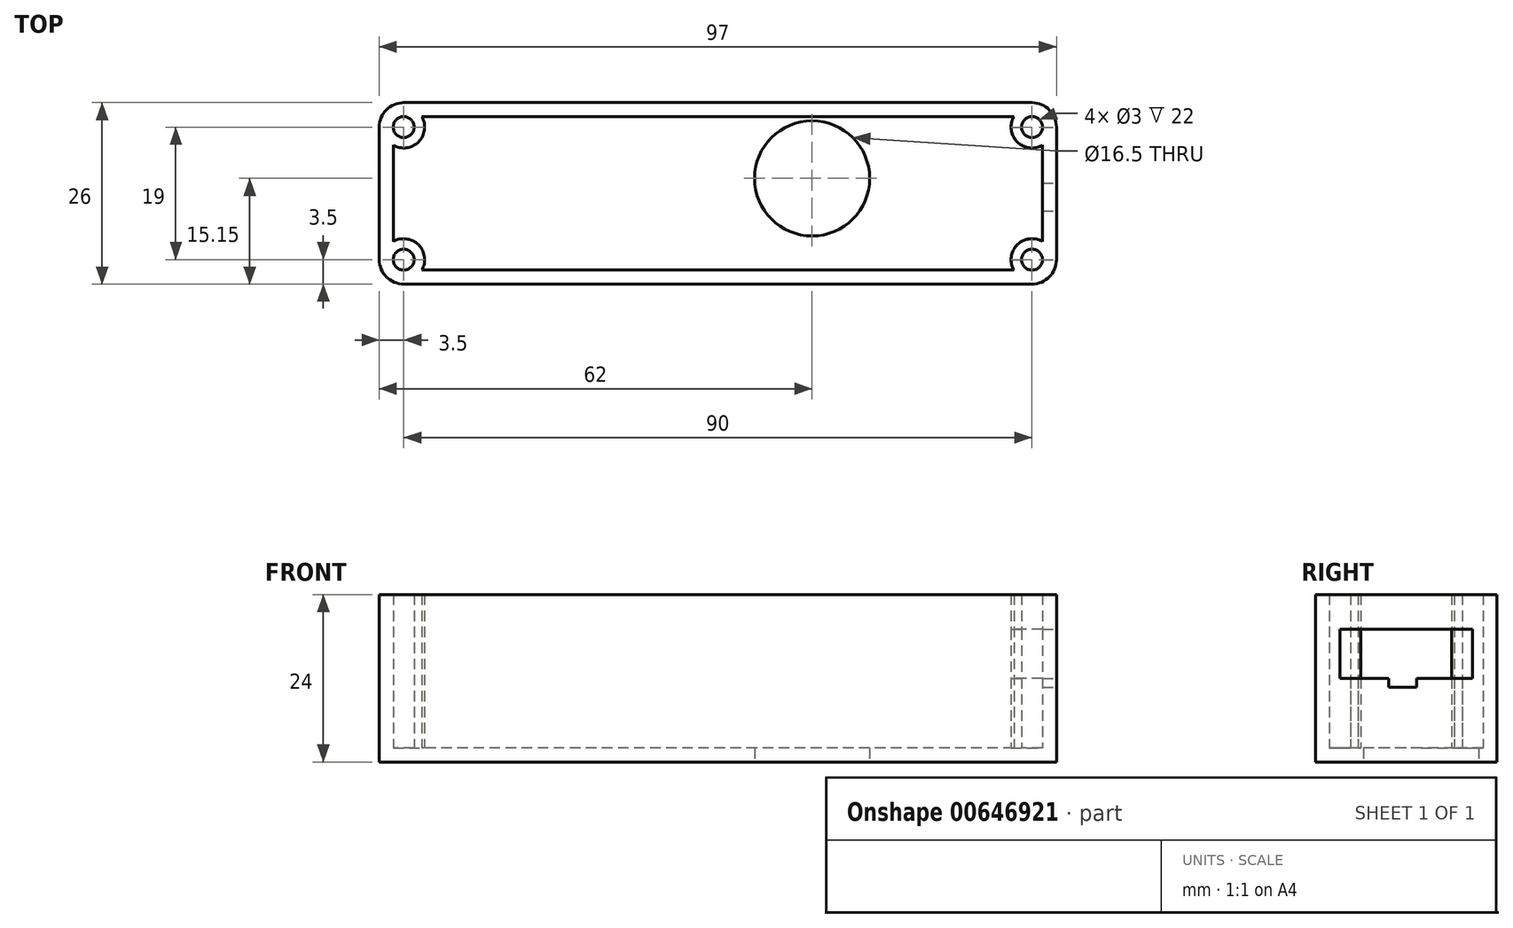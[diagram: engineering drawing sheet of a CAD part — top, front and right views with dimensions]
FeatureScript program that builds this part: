
annotation { "Feature Type Name" : "Feature", "Feature Type Description" : "" }
export const myFeature = defineFeature(function(context is Context, id is Id, definition is map)
    precondition{}
    {
        {
            var Q0;
            Q0=qCreatedBy(makeId("Top.planeOp"),FACE);
            var sketch = newSketch(context, id + "F0", { "sketchPlane" : qUnion([Q0])});
            skLineSegment(sketch, "E0.bottom", {"start": v(45, 13) * mm, "end": v(-45, 13) * mm});
            skLineSegment(sketch, "E0.top", {"start": v(45, -13) * mm, "end": v(-45, -13) * mm});
            skLineSegment(sketch, "E0.left", {"start": v(48.5, 9.5) * mm, "end": v(48.5, -9.5) * mm});
            skLineSegment(sketch, "E0.right", {"start": v(-48.5, 9.5) * mm, "end": v(-48.5, -9.5) * mm});
            skPoint(sketch, "E0.middle", {"position": v(0, 0) * mm});
            skPoint(sketch, "E1.visualSharp", {"position": v(48.5, 13) * mm});
            skArc(sketch, "E1.filletArc", {"start": v(48.5, 9.5) * mm, "mid": v(47.47, 11.97) * mm, "end": v(45, 13) * mm});
            skPoint(sketch, "E2.visualSharp", {"position": v(48.5, -13) * mm});
            skArc(sketch, "E2.filletArc", {"start": v(45, -13) * mm, "mid": v(47.47, -11.97) * mm, "end": v(48.5, -9.5) * mm});
            skPoint(sketch, "E3.visualSharp", {"position": v(-48.5, 13) * mm});
            skArc(sketch, "E3.filletArc", {"start": v(-45, 13) * mm, "mid": v(-47.47, 11.97) * mm, "end": v(-48.5, 9.5) * mm});
            skPoint(sketch, "E4.visualSharp", {"position": v(-48.5, -13) * mm});
            skArc(sketch, "E4.filletArc", {"start": v(-48.5, -9.5) * mm, "mid": v(-47.47, -11.97) * mm, "end": v(-45, -13) * mm});
            skSolve(sketch);
        }
        {
            var Q0;
            Q0=makeQuery(id+"F0.imprint","IMPRINT",FACE,{"disambiguationData":[TD([[makeQuery(id+"F0.imprint","IMPRINT",EDGE,{"derivedFrom":sQuery(id+"F0.wireOp",EDGE,"E0.bottom")}),1.0]])]});
            extrude(context, id + "F1", {"entities" : qUnion([Q0]), "depth" : 24 * mm, "offsetDistance" : 25 * mm});
        }
        {
            var Q0;
            Q0=makeQuery(id+"F1.opExtrude","CAP_FACE",FACE,{"disambiguationData":[OSD([sQuery(id+"F0.wireOp",EDGE,"E0.bottom"),sQuery(id+"F0.wireOp",EDGE,"E0.top"),sQuery(id+"F0.wireOp",EDGE,"E0.left"),sQuery(id+"F0.wireOp",EDGE,"E0.right")])],"isStart":false});
            shell(context, id + "F2", {"entities" : qUnion([Q0]), "thickness" : 2 * mm});
        }
        {
            var Q0;
            Q0=makeQuery(id+"F1.opExtrude","CAP_FACE",FACE,{"disambiguationData":[OSD([sQuery(id+"F0.wireOp",EDGE,"E0.bottom"),sQuery(id+"F0.wireOp",EDGE,"E0.top"),sQuery(id+"F0.wireOp",EDGE,"E0.left"),sQuery(id+"F0.wireOp",EDGE,"E0.right")])],"isStart":true});
            var sketch = newSketch(context, id + "F3", { "sketchPlane" : qUnion([Q0])});
            skCircle(sketch, "E5", {"center": v(13.5, -2.15) * mm, "radius": 8.25 * mm});
            skSolve(sketch);
        }
        {
            var Q0;
            Q0 = qSketchRegion(id + "F3", true);
            var Q1;
            Q1=makeQuery(id+"F2.opShell","OFFSET_FACE",FACE,{"disambiguationData":[OSD([sQuery(id+"F0.wireOp",EDGE,"E0.bottom"),sQuery(id+"F0.wireOp",EDGE,"E0.top"),sQuery(id+"F0.wireOp",EDGE,"E0.left"),sQuery(id+"F0.wireOp",EDGE,"E0.right")])]});
            extrude(context, id + "F4", {"entities" : qUnion([Q0]), "operationType" : NewBodyOperationType.REMOVE, "endBound" : BoundingType.UP_TO_SURFACE, "oppositeDirection" : true, "depth" : 25 * mm, "endBoundEntityFace" : qUnion([Q1]), "offsetDistance" : 25 * mm});
        }
        {
            var Q0;
            Q0=makeQuery(id+"F2.opShell","OFFSET_FACE",FACE,{"disambiguationData":[OSD([sQuery(id+"F0.wireOp",EDGE,"E0.bottom"),sQuery(id+"F0.wireOp",EDGE,"E0.top"),sQuery(id+"F0.wireOp",EDGE,"E0.left"),sQuery(id+"F0.wireOp",EDGE,"E0.right")])]});
            var sketch = newSketch(context, id + "F5", { "sketchPlane" : qUnion([Q0])});
            skCircle(sketch, "E6", {"center": v(-45, 9.5) * mm, "radius": 3 * mm});
            skCircle(sketch, "E7.0", {"center": v(-45, 9.5) * mm, "radius": 1.5 * mm});
            skCircle(sketch, "E8.MirrorC", {"center": v(45, 9.5) * mm, "radius": 3 * mm});
            skCircle(sketch, "E9.MirrorC", {"center": v(45, 9.5) * mm, "radius": 1.5 * mm});
            skCircle(sketch, "E10.MirrorC", {"center": v(-45, -9.5) * mm, "radius": 3 * mm});
            skCircle(sketch, "E11.MirrorC", {"center": v(-45, -9.5) * mm, "radius": 1.5 * mm});
            skCircle(sketch, "E12.MirrorC", {"center": v(45, -9.5) * mm, "radius": 1.5 * mm});
            skCircle(sketch, "E13.MirrorC", {"center": v(45, -9.5) * mm, "radius": 3 * mm});
            skSolve(sketch);
        }
        {
            var Q0;
            Q0 = qSketchRegion(id + "F5", true);
            var Q1;
            Q1=makeQuery(id+"F1.opExtrude","CAP_FACE",FACE,{"disambiguationData":[OSD([sQuery(id+"F0.wireOp",EDGE,"E0.bottom"),sQuery(id+"F0.wireOp",EDGE,"E0.top"),sQuery(id+"F0.wireOp",EDGE,"E0.left"),sQuery(id+"F0.wireOp",EDGE,"E0.right")])],"isStart":false});
            extrude(context, id + "F6", {"entities" : qUnion([Q0]), "operationType" : NewBodyOperationType.ADD, "endBound" : BoundingType.UP_TO_SURFACE, "depth" : 25 * mm, "endBoundEntityFace" : qUnion([Q1]), "offsetDistance" : 25 * mm});
        }
        {
            var Q0;
            Q0=makeQuery(id+"F1.opExtrude","SWEPT_FACE",FACE,{"disambiguationData":[OSD([sQuery(id+"F0.wireOp",EDGE,"E0.left")])]});
            var sketch = newSketch(context, id + "F7", { "sketchPlane" : qUnion([Q0])});
            skLineSegment(sketch, "E14.bottom", {"start": v(-9.5, 12) * mm, "end": v(9.5, 12) * mm, "construction": true});
            skLineSegment(sketch, "E14.top", {"start": v(-9.5, 19) * mm, "end": v(9.5, 19) * mm});
            skLineSegment(sketch, "E14.left", {"start": v(-9.5, 12) * mm, "end": v(-9.5, 19) * mm});
            skLineSegment(sketch, "E14.right", {"start": v(9.5, 12) * mm, "end": v(9.5, 19) * mm});
            skLineSegment(sketch, "E15", {"start": v(-2.5, 12) * mm, "end": v(-2.5, 10.7) * mm});
            skLineSegment(sketch, "E16", {"start": v(-2.5, 10.7) * mm, "end": v(1.5, 10.7) * mm});
            skLineSegment(sketch, "E17", {"start": v(1.5, 10.7) * mm, "end": v(1.5, 12) * mm});
            skLineSegment(sketch, "E18", {"start": v(-9.5, 12) * mm, "end": v(-2.5, 12) * mm});
            skLineSegment(sketch, "E19", {"start": v(1.5, 12) * mm, "end": v(9.5, 12) * mm});
            skSolve(sketch);
        }
        {
            var Q0;
            Q0 = qSketchRegion(id + "F7", true);
            var Q1;
            Q1=makeQuery(id+"F2.opShell","OFFSET_FACE",FACE,{"disambiguationData":[OSD([sQuery(id+"F0.wireOp",EDGE,"E0.left")])]});
            extrude(context, id + "F8", {"entities" : qUnion([Q0]), "operationType" : NewBodyOperationType.REMOVE, "oppositeDirection" : true, "depth" : 10 * mm, "endBoundEntityFace" : qUnion([Q1]), "offsetDistance" : 25 * mm});
        }
    });
